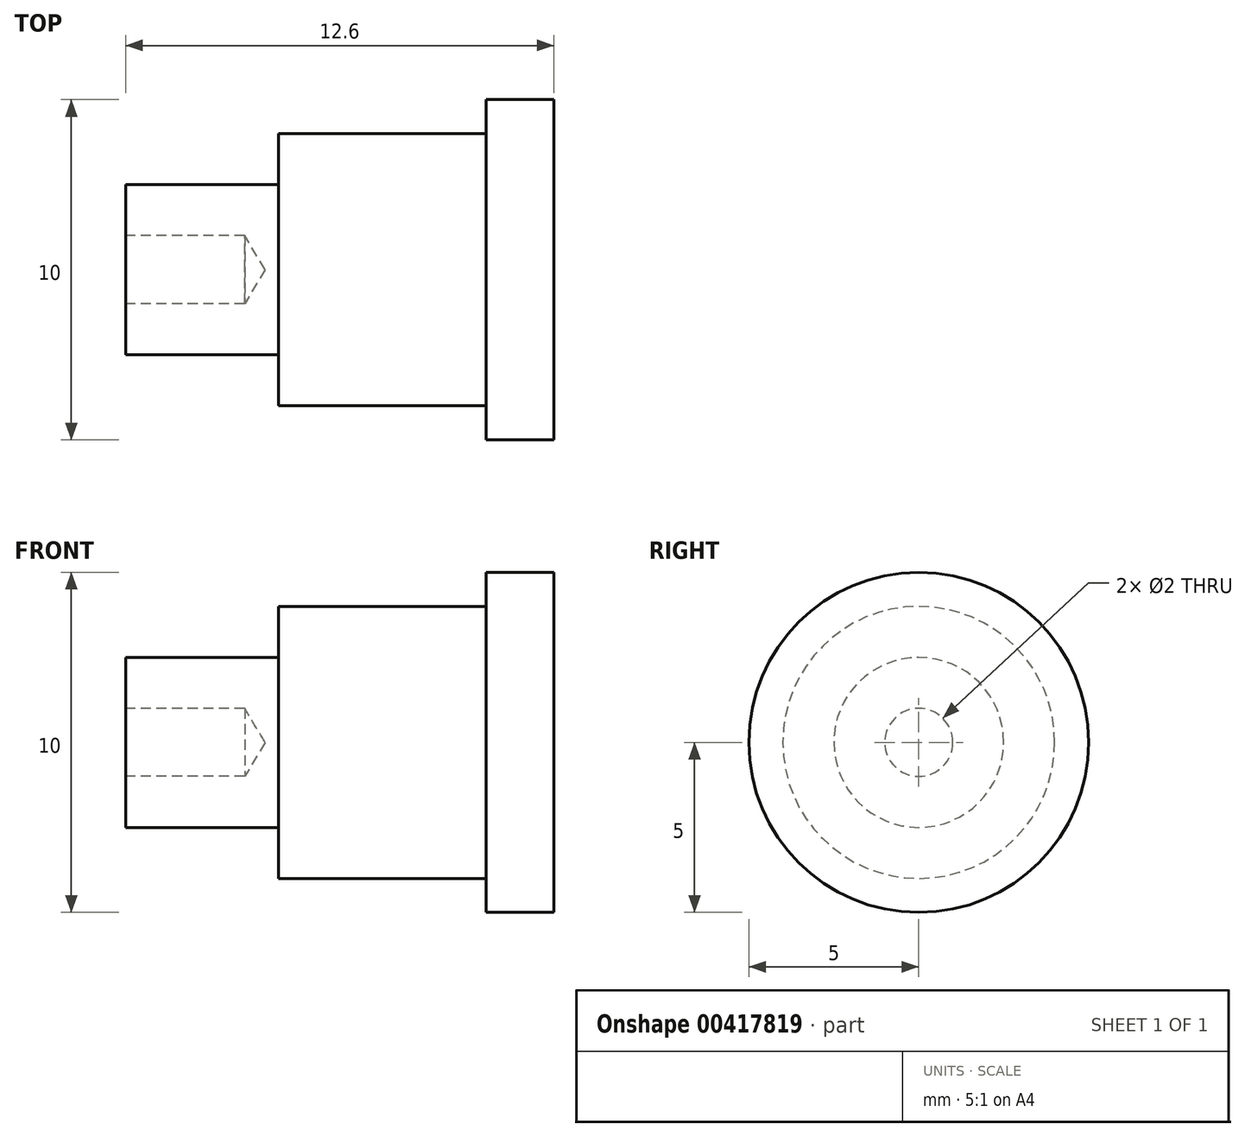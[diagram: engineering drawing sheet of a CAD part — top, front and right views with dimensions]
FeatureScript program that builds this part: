
annotation { "Feature Type Name" : "Feature", "Feature Type Description" : "" }
export const myFeature = defineFeature(function(context is Context, id is Id, definition is map)
    precondition{}
    {
        {
            var Q0;
            Q0=qCreatedBy(makeId("Front.planeOp"),FACE);
            var sketch = newSketch(context, id + "F0", { "sketchPlane" : qUnion([Q0])});
            skLineSegment(sketch, "E0", {"start": v(0, 0) * mm, "end": v(0, 5) * mm});
            skLineSegment(sketch, "E1", {"start": v(0, 5) * mm, "end": v(-2, 5) * mm});
            skLineSegment(sketch, "E2", {"start": v(-2, 5) * mm, "end": v(-2, 4) * mm});
            skLineSegment(sketch, "E3", {"start": v(-2, 4) * mm, "end": v(-8.1, 4) * mm});
            skLineSegment(sketch, "E4", {"start": v(-8.1, 4) * mm, "end": v(-8.1, 2.5) * mm});
            skLineSegment(sketch, "E5", {"start": v(-8.1, 2.5) * mm, "end": v(-12.6, 2.5) * mm});
            skLineSegment(sketch, "E6", {"start": v(-12.6, 2.5) * mm, "end": v(-12.6, 0) * mm});
            skLineSegment(sketch, "E7", {"start": v(-12.6, 0) * mm, "end": v(0, 0) * mm});
            skSolve(sketch);
        }
        {
            var Q0;
            Q0=makeQuery(id+"F0.imprint","IMPRINT",FACE,{"disambiguationData":[TD([[makeQuery(id+"F0.imprint","IMPRINT",EDGE,{"derivedFrom":sQuery(id+"F0.wireOp",EDGE,"E0")}),1.0]])]});
            var Q1;
            Q1=sQuery(id+"F0.wireOp",EDGE,"E7");
            revolve(context, id + "F1", {"entities" : qUnion([Q0]), "axis" : qUnion([Q1]), "revolveType" : RevolveType.FULL});
        }
        {
            var Q0;
            Q0=makeQuery(id+"F1.opRevolve","SWEPT_FACE",FACE,{"disambiguationData":[OSD([sQuery(id+"F0.wireOp",EDGE,"E6")])]});
            var sketch = newSketch(context, id + "F2", { "sketchPlane" : qUnion([Q0])});
            skPoint(sketch, "E8.0", {"position": v(0, 0) * mm});
            skSolve(sketch);
        }
        {
            var Q0;
            Q0=sQuery(id+"F2.wireOp",VERTEX,"E8.0");
            var Q1;
            Q1=makeQuery(id+"F1.opRevolve","SWEPT_BODY",BODY,{"disambiguationData":[OSD([sQuery(id+"F0.wireOp",EDGE,"E0"),sQuery(id+"F0.wireOp",EDGE,"E1"),sQuery(id+"F0.wireOp",EDGE,"E2"),sQuery(id+"F0.wireOp",EDGE,"E3"),sQuery(id+"F0.wireOp",EDGE,"E4"),sQuery(id+"F0.wireOp",EDGE,"E5"),sQuery(id+"F0.wireOp",EDGE,"E6"),sQuery(id+"F0.wireOp",EDGE,"E7")])]});
            hole(context, id + "F3", {"style" : HoleStyle.SIMPLE, "endStyle" : HoleEndStyle.BLIND, "holeDiameter" : 2 * mm, "holeDepth" : 3.5 * mm, "isTappedThrough" : true, "tappedDepth" : 19.25 * mm, "tapClearance" : 3, "startFromSketch" : true, "locations" : qUnion([Q0]), "scope" : qUnion([Q1])});
        }
    });
